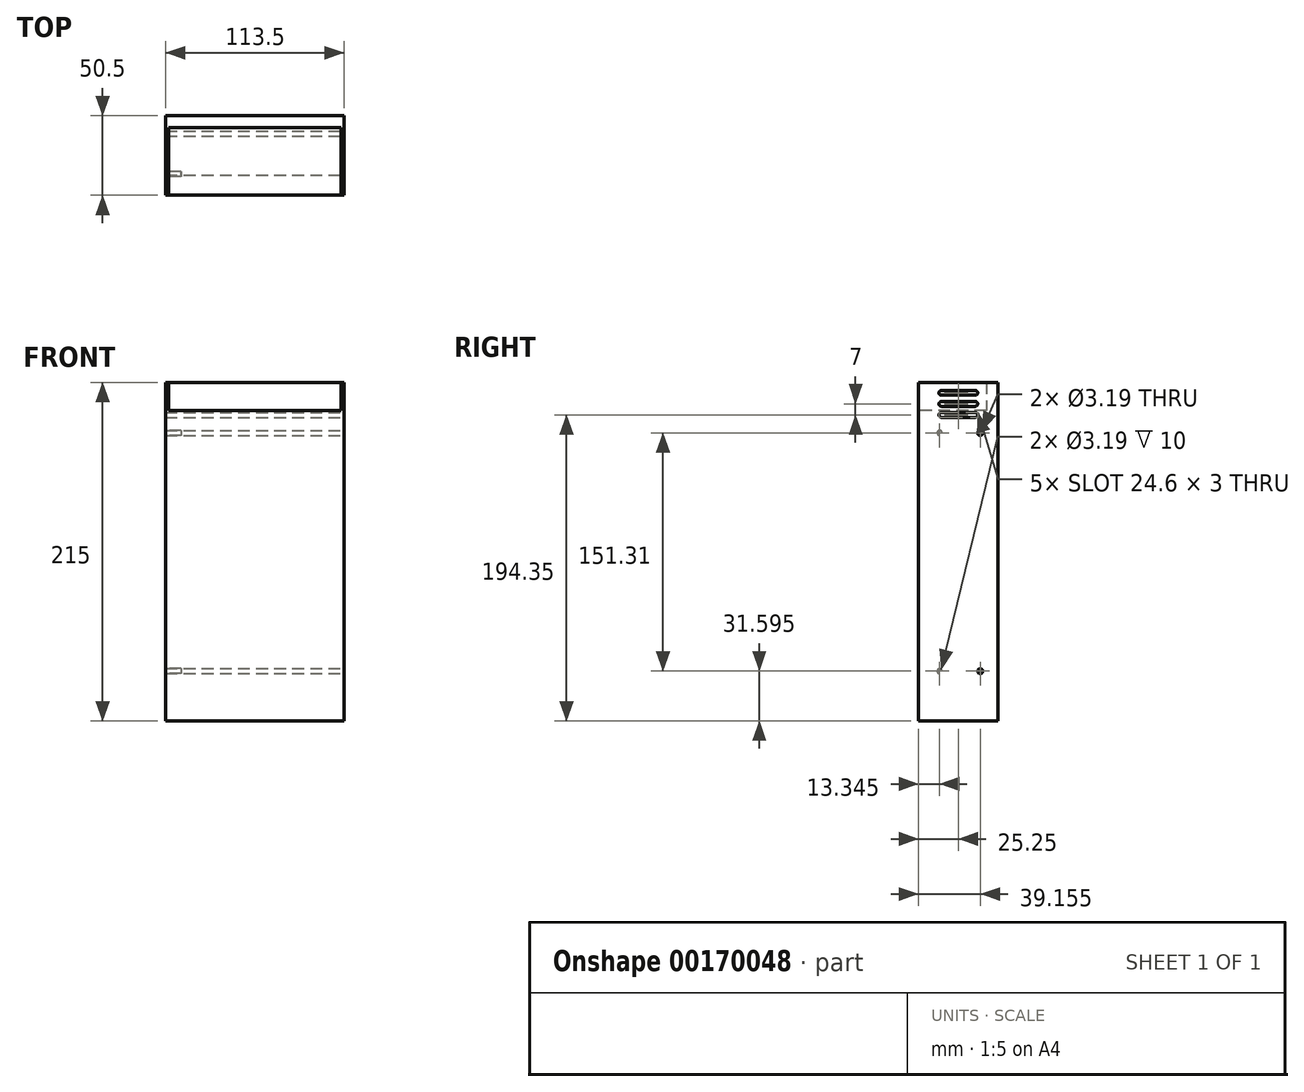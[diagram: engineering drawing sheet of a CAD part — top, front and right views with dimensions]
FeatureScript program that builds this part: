
annotation { "Feature Type Name" : "Feature", "Feature Type Description" : "" }
export const myFeature = defineFeature(function(context is Context, id is Id, definition is map)
    precondition{}
    {
        {
            var Q0;
            Q0=qCreatedBy(makeId("Top.planeOp"),FACE);
            var sketch = newSketch(context, id + "F0", { "sketchPlane" : qUnion([Q0])});
            skLineSegment(sketch, "E0.bottom", {"start": v(0, 0) * mm, "end": v(113.5, 0) * mm});
            skLineSegment(sketch, "E0.top", {"start": v(0, 50.5) * mm, "end": v(113.5, 50.5) * mm});
            skLineSegment(sketch, "E0.left", {"start": v(0, 0) * mm, "end": v(0, 50.5) * mm});
            skLineSegment(sketch, "E0.right", {"start": v(113.5, 0) * mm, "end": v(113.5, 50.5) * mm});
            skSolve(sketch);
        }
        {
            var Q0;
            Q0 = qSketchRegion(id + "F0", true);
            extrude(context, id + "F1", {"entities" : qUnion([Q0]), "depth" : 215 * mm});
        }
        {
            var Q0;
            Q0=makeQuery(id+"F1.opExtrude","SWEPT_FACE",FACE,{"disambiguationData":[OSD([sQuery(id+"F0.wireOp",EDGE,"E0.right")])]});
            var sketch = newSketch(context, id + "F2", { "sketchPlane" : qUnion([Q0])});
            skLineSegment(sketch, "E1.bottom", {"start": v(14.45, 209.85) * mm, "end": v(36.05, 209.85) * mm});
            skLineSegment(sketch, "E1.top", {"start": v(14.45, 206.85) * mm, "end": v(36.05, 206.85) * mm});
            skLineSegment(sketch, "E1.left", {"start": v(12.95, 208.35) * mm, "end": v(12.95, 208.35) * mm});
            skLineSegment(sketch, "E1.right", {"start": v(37.55, 208.35) * mm, "end": v(37.55, 208.35) * mm});
            skPoint(sketch, "E2.visualSharp", {"position": v(12.95, 209.85) * mm});
            skArc(sketch, "E2.filletArc", {"start": v(14.45, 209.85) * mm, "mid": v(13.39, 209.41) * mm, "end": v(12.95, 208.35) * mm});
            skPoint(sketch, "E3.visualSharp", {"position": v(12.95, 206.85) * mm});
            skArc(sketch, "E3.filletArc", {"start": v(12.95, 208.35) * mm, "mid": v(13.39, 207.29) * mm, "end": v(14.45, 206.85) * mm});
            skPoint(sketch, "E4.visualSharp", {"position": v(37.55, 209.85) * mm});
            skArc(sketch, "E4.filletArc", {"start": v(37.55, 208.35) * mm, "mid": v(37.11, 209.41) * mm, "end": v(36.05, 209.85) * mm});
            skPoint(sketch, "E5.visualSharp", {"position": v(37.55, 206.85) * mm});
            skArc(sketch, "E5.filletArc", {"start": v(36.05, 206.85) * mm, "mid": v(37.11, 207.29) * mm, "end": v(37.55, 208.35) * mm});
            skPoint(sketch, "E6.1.0.0", {"position": v(37.55, 199.85) * mm});
            skPoint(sketch, "E6.1.0.1", {"position": v(12.95, 202.85) * mm});
            skPoint(sketch, "E6.1.0.2", {"position": v(37.55, 202.85) * mm});
            skLineSegment(sketch, "E6.1.0.3", {"start": v(14.45, 199.85) * mm, "end": v(36.05, 199.85) * mm});
            skLineSegment(sketch, "E6.1.0.4", {"start": v(14.45, 202.85) * mm, "end": v(36.05, 202.85) * mm});
            skPoint(sketch, "E6.1.0.5", {"position": v(12.95, 199.85) * mm});
            skArc(sketch, "E6.1.0.6", {"start": v(12.95, 201.35) * mm, "mid": v(13.39, 200.29) * mm, "end": v(14.45, 199.85) * mm});
            skArc(sketch, "E6.1.0.7", {"start": v(37.55, 201.35) * mm, "mid": v(37.11, 202.41) * mm, "end": v(36.05, 202.85) * mm});
            skArc(sketch, "E6.1.0.8", {"start": v(36.05, 199.85) * mm, "mid": v(37.11, 200.29) * mm, "end": v(37.55, 201.35) * mm});
            skArc(sketch, "E6.1.0.9", {"start": v(14.45, 202.85) * mm, "mid": v(13.39, 202.41) * mm, "end": v(12.95, 201.35) * mm});
            skPoint(sketch, "E6.2.0.0", {"position": v(37.55, 192.85) * mm});
            skPoint(sketch, "E6.2.0.1", {"position": v(12.95, 195.85) * mm});
            skPoint(sketch, "E6.2.0.2", {"position": v(37.55, 195.85) * mm});
            skLineSegment(sketch, "E6.2.0.3", {"start": v(14.45, 192.85) * mm, "end": v(36.05, 192.85) * mm});
            skLineSegment(sketch, "E6.2.0.4", {"start": v(14.45, 195.85) * mm, "end": v(36.05, 195.85) * mm});
            skPoint(sketch, "E6.2.0.5", {"position": v(12.95, 192.85) * mm});
            skArc(sketch, "E6.2.0.6", {"start": v(12.95, 194.35) * mm, "mid": v(13.39, 193.29) * mm, "end": v(14.45, 192.85) * mm});
            skArc(sketch, "E6.2.0.7", {"start": v(37.55, 194.35) * mm, "mid": v(37.11, 195.41) * mm, "end": v(36.05, 195.85) * mm});
            skArc(sketch, "E6.2.0.8", {"start": v(36.05, 192.85) * mm, "mid": v(37.11, 193.29) * mm, "end": v(37.55, 194.35) * mm});
            skArc(sketch, "E6.2.0.9", {"start": v(14.45, 195.85) * mm, "mid": v(13.39, 195.41) * mm, "end": v(12.95, 194.35) * mm});
            skLineSegment(sketch, "E6.direction1", {"start": v(12.95, 206.85) * mm, "end": v(12.95, 199.85) * mm, "construction": true});
            skSolve(sketch);
        }
        {
            var Q0;
            Q0=makeQuery(id+"F2.imprint","IMPRINT",FACE,{"disambiguationData":[TD([[makeQuery(id+"F2.imprint","IMPRINT",EDGE,{"derivedFrom":sQuery(id+"F2.wireOp",EDGE,"E1.bottom")}),-1.0]])]});
            var Q1;
            Q1=makeQuery(id+"F2.imprint","IMPRINT",FACE,{"disambiguationData":[TD([[makeQuery(id+"F2.imprint","IMPRINT",EDGE,{"derivedFrom":sQuery(id+"F2.wireOp",EDGE,"E6.1.0.3")}),1.0]])]});
            var Q2;
            Q2=makeQuery(id+"F2.imprint","IMPRINT",FACE,{"disambiguationData":[TD([[makeQuery(id+"F2.imprint","IMPRINT",EDGE,{"derivedFrom":sQuery(id+"F2.wireOp",EDGE,"E6.2.0.3")}),1.0]])]});
            extrude(context, id + "F3", {"entities" : qUnion([Q0, Q1, Q2]), "operationType" : NewBodyOperationType.REMOVE, "endBound" : BoundingType.THROUGH_ALL, "oppositeDirection" : true, "depth" : 25 * mm});
        }
        {
            var Q0;
            Q0=makeQuery(id+"F1.opExtrude","SWEPT_FACE",FACE,{"disambiguationData":[OSD([sQuery(id+"F0.wireOp",EDGE,"E0.bottom")])]});
            var sketch = newSketch(context, id + "F4", { "sketchPlane" : qUnion([Q0])});
            skLineSegment(sketch, "E7", {"start": v(111.5, 215) * mm, "end": v(111.5, 197) * mm});
            skLineSegment(sketch, "E8", {"start": v(2, 215) * mm, "end": v(2, 197) * mm});
            skLineSegment(sketch, "E9", {"start": v(2, 197) * mm, "end": v(111.5, 197) * mm});
            skSolve(sketch);
        }
        {
            var Q0;
            {var subQ0=sQuery(id+"F4.wireOp",EDGE,"E7");Q0=makeQuery(id+"F4.imprint","IMPRINT",FACE,{"disambiguationData":[TD([[makeQuery(id+"F4.imprint","IMPRINT",EDGE,{"derivedFrom":subQ0}),-1.0]])]});}
            extrude(context, id + "F5", {"entities" : qUnion([Q0]), "operationType" : NewBodyOperationType.REMOVE, "oppositeDirection" : true, "depth" : (50.5 - 7.5) * mm});
        }
        {
            var Q0;
            Q0=makeQuery(id+"F1.opExtrude","SWEPT_FACE",FACE,{"disambiguationData":[OSD([sQuery(id+"F0.wireOp",EDGE,"E0.right")])]});
            var sketch = newSketch(context, id + "F6", { "sketchPlane" : qUnion([Q0])});
            skCircle(sketch, "E10", {"center": v(39.15, 182.9) * mm, "radius": 1.6 * mm});
            skCircle(sketch, "E11", {"center": v(39.15, 31.6) * mm, "radius": 1.6 * mm});
            skSolve(sketch);
        }
        {
            var Q0;
            Q0=makeQuery(id+"F6.imprint","IMPRINT",FACE,{"disambiguationData":[TD([[makeQuery(id+"F6.imprint","IMPRINT",EDGE,{"derivedFrom":sQuery(id+"F6.wireOp",EDGE,"E11")}),1.0]])]});
            var Q1;
            Q1=makeQuery(id+"F6.imprint","IMPRINT",FACE,{"disambiguationData":[TD([[makeQuery(id+"F6.imprint","IMPRINT",EDGE,{"derivedFrom":sQuery(id+"F6.wireOp",EDGE,"E10")}),1.0]])]});
            extrude(context, id + "F7", {"entities" : qUnion([Q0, Q1]), "operationType" : NewBodyOperationType.REMOVE, "endBound" : BoundingType.THROUGH_ALL, "oppositeDirection" : true, "depth" : 10 * mm});
        }
        {
            var Q0;
            Q0=makeQuery(id+"F1.opExtrude","SWEPT_FACE",FACE,{"disambiguationData":[OSD([sQuery(id+"F0.wireOp",EDGE,"E0.left")])]});
            var sketch = newSketch(context, id + "F8", { "sketchPlane" : qUnion([Q0])});
            skCircle(sketch, "E12", {"center": v(-13.34, 182.9) * mm, "radius": 1.6 * mm});
            skCircle(sketch, "E13", {"center": v(-13.34, 31.6) * mm, "radius": 1.6 * mm});
            skSolve(sketch);
        }
        {
            var Q0;
            Q0 = qSketchRegion(id + "F8", true);
            extrude(context, id + "F9", {"entities" : qUnion([Q0]), "operationType" : NewBodyOperationType.REMOVE, "oppositeDirection" : true, "depth" : 10 * mm});
        }
    });
